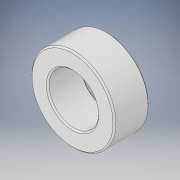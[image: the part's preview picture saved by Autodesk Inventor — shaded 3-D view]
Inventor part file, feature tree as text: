
AUTODESK INVENTOR PART (.ipt)
format: ipt  version: 2019 (Build 230136000, 136)  size: 117,760 bytes
history: native  units: in
note: dims shown in document units (in); Inventor stores cm internally (conversion verified against a paired STEP export)
features: sketch x2, extrude x1, chamfer x1
ambient origin geometry x8: Origin, YZ Plane, XZ Plane, XY Plane, X Axis, Y Axis, Z Axis, Center Point
bodies: Solid1 (feature_tree)
feature tree (4):
  extrude  "Extrusion1"  Depth=0.375in
  chamfer  "Chamfer1"  Distance=0.375in
  sketch  "Sketch2"  dims[d4=0.0157in d5=0.125in d6=45.0deg]
  sketch  "Sketch1"  dims[d0=0.9in d1=0.5312in d2=0.375in d3=0.0in]
